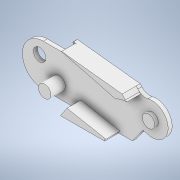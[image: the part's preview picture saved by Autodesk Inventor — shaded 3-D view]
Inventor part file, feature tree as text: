
AUTODESK INVENTOR PART (.ipt)
format: ipt  version: 2022 (Build 260153000, 153)  size: 196,096 bytes
history: native  units: in
note: dims shown in document units (in); Inventor stores cm internally (conversion verified against a paired STEP export)
features: extrude x5, sketch x5, other x1
ambient origin geometry x8: Origin, YZ Plane, XZ Plane, XY Plane, X Axis, Y Axis, Z Axis, Center Point
bodies: Body1 (feature_tree)
feature tree (11):
  other  "Sólido1"
  extrude  "Extrusión1"  Depth=0.3307in
  extrude  "Extrusión2"  Depth=0.1102in TaperAngle=0.0deg
  extrude  "Extrusión3"  Depth=0.0591in TaperAngle=0.0deg
  extrude  "Extrusión4"  Depth=0.0787in
  extrude  "Extrusión5"  [1 undecoded]
  sketch  "Boceto1"  dims[d1=0.0984in d6=0.3307in]
  sketch  "Boceto2"  dims[d18=0.0315in d19=0.0in d24=0.1102in d25=0.0in]
  sketch  "Boceto3"  dims[d26=0.0591in d27=0.0in d28=0.0394in d29=0.0in]
  sketch  "Boceto4"  dims[d31=0.0472in d32=0.0in d33=0.0787in]
  sketch  "Boceto5"
note: 1 required parameter value undecoded (feature->parameter linkage not recoverable at this tier; creation-order binding heuristic only, values carry confidence <= 0.55)
